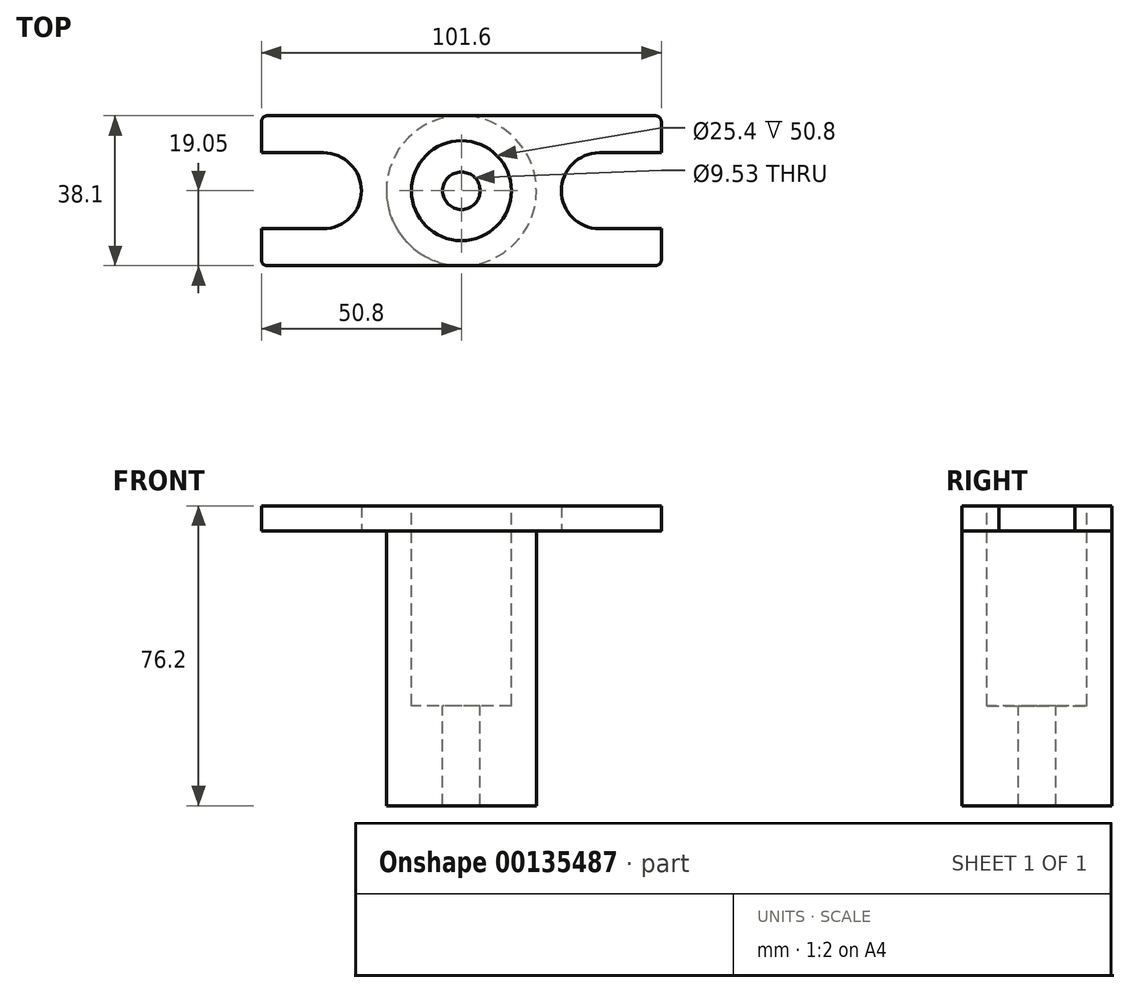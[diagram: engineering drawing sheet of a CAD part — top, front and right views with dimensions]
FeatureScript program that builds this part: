
annotation { "Feature Type Name" : "Feature", "Feature Type Description" : "" }
export const myFeature = defineFeature(function(context is Context, id is Id, definition is map)
    precondition{}
    {
        {
            var Q0;
            Q0=qCreatedBy(makeId("Top.planeOp"),FACE);
            var sketch = newSketch(context, id + "F0", { "sketchPlane" : qUnion([Q0])});
            skLineSegment(sketch, "E0.bottom", {"start": v(0, 0) * mm, "end": v(101.6, 0) * mm});
            skLineSegment(sketch, "E0.top", {"start": v(0, 38.1) * mm, "end": v(101.6, 38.1) * mm});
            skLineSegment(sketch, "E0.left", {"start": v(0, 0) * mm, "end": v(0, 9.4) * mm});
            skLineSegment(sketch, "E0.right", {"start": v(101.6, 0) * mm, "end": v(101.6, 9.4) * mm});
            skLineSegment(sketch, "E1.trimOffspring", {"start": v(0, 28.7) * mm, "end": v(0, 38.1) * mm});
            skLineSegment(sketch, "E2.trimOffspring", {"start": v(101.6, 28.7) * mm, "end": v(101.6, 38.1) * mm});
            skLineSegment(sketch, "E3.bottom", {"start": v(0, 28.7) * mm, "end": v(15.75, 28.7) * mm});
            skLineSegment(sketch, "E3.top", {"start": v(0, 9.4) * mm, "end": v(15.75, 9.4) * mm});
            skLineSegment(sketch, "E3.left", {"start": v(0, 28.7) * mm, "end": v(0, 9.4) * mm});
            skLineSegment(sketch, "E3.right", {"start": v(15.75, 28.7) * mm, "end": v(15.75, 9.4) * mm});
            skLineSegment(sketch, "E4.bottom", {"start": v(101.6, 28.7) * mm, "end": v(85.85, 28.7) * mm});
            skLineSegment(sketch, "E4.top", {"start": v(101.6, 9.4) * mm, "end": v(85.85, 9.4) * mm});
            skLineSegment(sketch, "E4.left", {"start": v(101.6, 28.7) * mm, "end": v(101.6, 9.4) * mm});
            skLineSegment(sketch, "E4.right", {"start": v(85.85, 28.7) * mm, "end": v(85.85, 9.4) * mm});
            skArc(sketch, "E5", {"start": v(15.75, 9.4) * mm, "mid": v(25.4, 19.05) * mm, "end": v(15.75, 28.7) * mm});
            skArc(sketch, "E6", {"start": v(85.85, 28.7) * mm, "mid": v(76.2, 19.05) * mm, "end": v(85.85, 9.4) * mm});
            skCircle(sketch, "E7", {"center": v(50.8, 19.93) * mm, "radius": 8.78 * mm, "construction": true});
            skSolve(sketch);
        }
        {
            var Q0;
            Q0=makeQuery(id+"F0.imprint","IMPRINT",FACE,{"disambiguationData":[TD([[makeQuery(id+"F0.imprint","IMPRINT",EDGE,{"derivedFrom":sQuery(id+"F0.wireOp",EDGE,"E0.bottom")}),1.0]])]});
            extrude(context, id + "F1", {"entities" : qUnion([Q0]), "depth" : 6.35 * mm});
        }
        {
            var Q0;
            Q0=makeQuery(id+"F1.opExtrude","CAP_FACE",FACE,{"disambiguationData":[OSD([sQuery(id+"F0.wireOp",EDGE,"E0.bottom"),sQuery(id+"F0.wireOp",EDGE,"E0.top"),sQuery(id+"F0.wireOp",EDGE,"E0.left"),sQuery(id+"F0.wireOp",EDGE,"E0.right"),sQuery(id+"F0.wireOp",EDGE,"So8w0W6L-Nd8J-bDPT-vjVD-5eYZ7nEJATCC"),sQuery(id+"F0.wireOp",EDGE,"ML5IMY0P-KDOL-A0Oi-dJc1-0zr9aFNHKgkh"),sQuery(id+"F0.wireOp",EDGE,"E1.trimOffspring"),sQuery(id+"F0.wireOp",EDGE,"E2.trimOffspring")])],"isStart":true});
            var sketch = newSketch(context, id + "F2", { "sketchPlane" : qUnion([Q0])});
            skCircle(sketch, "E8", {"center": v(50.8, -19.05) * mm, "radius": 19.05 * mm});
            skSolve(sketch);
        }
        {
            var Q0;
            Q0=makeQuery(id+"F2.imprint","IMPRINT",FACE,{"disambiguationData":[TD([[makeQuery(id+"F2.imprint","IMPRINT",EDGE,{"derivedFrom":sQuery(id+"F2.wireOp",EDGE,"E8")}),1.0]])]});
            extrude(context, id + "F3", {"entities" : qUnion([Q0]), "operationType" : NewBodyOperationType.ADD, "depth" : 69.85 * mm});
        }
        {
            var Q0;
            Q0=makeQuery(id+"F1.opExtrude","CAP_FACE",FACE,{"disambiguationData":[OSD([sQuery(id+"F0.wireOp",EDGE,"E0.bottom"),sQuery(id+"F0.wireOp",EDGE,"E0.top"),sQuery(id+"F0.wireOp",EDGE,"E0.left"),sQuery(id+"F0.wireOp",EDGE,"E0.right"),sQuery(id+"F0.wireOp",EDGE,"So8w0W6L-Nd8J-bDPT-vjVD-5eYZ7nEJATCC"),sQuery(id+"F0.wireOp",EDGE,"ML5IMY0P-KDOL-A0Oi-dJc1-0zr9aFNHKgkh"),sQuery(id+"F0.wireOp",EDGE,"E1.trimOffspring"),sQuery(id+"F0.wireOp",EDGE,"E2.trimOffspring")])],"isStart":false});
            var sketch = newSketch(context, id + "F4", { "sketchPlane" : qUnion([Q0])});
            skCircle(sketch, "E9", {"center": v(50.8, 19.05) * mm, "radius": 12.7 * mm});
            skCircle(sketch, "E10", {"center": v(50.8, 19.05) * mm, "radius": 4.76 * mm});
            skSolve(sketch);
        }
        {
            var Q0;
            Q0=makeQuery(id+"F4.imprint","IMPRINT",FACE,{"disambiguationData":[TD([[makeQuery(id+"F4.imprint","IMPRINT",EDGE,{"derivedFrom":sQuery(id+"F4.wireOp",EDGE,"E9")}),1.0]])]});
            extrude(context, id + "F5", {"entities" : qUnion([Q0]), "operationType" : NewBodyOperationType.REMOVE, "oppositeDirection" : true, "depth" : 50.8 * mm});
        }
        {
            var Q0;
            Q0=makeQuery(id+"F4.imprint","IMPRINT",FACE,{"disambiguationData":[TD([[makeQuery(id+"F4.imprint","IMPRINT",EDGE,{"derivedFrom":sQuery(id+"F4.wireOp",EDGE,"E10")}),1.0]])]});
            extrude(context, id + "F6", {"entities" : qUnion([Q0]), "operationType" : NewBodyOperationType.REMOVE, "endBound" : BoundingType.THROUGH_ALL, "oppositeDirection" : true, "depth" : 25.4 * mm});
        }
        {
            var Q0;
            Q0=makeQuery(id+"F1.opExtrude","SWEPT_EDGE",EDGE,{"disambiguationData":[OSD([sQuery(id+"F0.wireOp",EDGE,"E0.top"),sQuery(id+"F0.wireOp",EDGE,"E1.trimOffspring")])]});
            var Q1;
            Q1=makeQuery(id+"F1.opExtrude","SWEPT_EDGE",EDGE,{"disambiguationData":[OSD([sQuery(id+"F0.wireOp",EDGE,"E0.bottom"),sQuery(id+"F0.wireOp",EDGE,"E0.left")])]});
            var Q2;
            Q2=makeQuery(id+"F1.opExtrude","SWEPT_EDGE",EDGE,{"disambiguationData":[OSD([sQuery(id+"F0.wireOp",EDGE,"E0.bottom"),sQuery(id+"F0.wireOp",EDGE,"E0.right")])]});
            var Q3;
            Q3=makeQuery(id+"F1.opExtrude","SWEPT_EDGE",EDGE,{"disambiguationData":[OSD([sQuery(id+"F0.wireOp",EDGE,"E0.top"),sQuery(id+"F0.wireOp",EDGE,"E2.trimOffspring")])]});
            fillet(context, id + "F7", {"entities" : qUnion([Q0, Q1, Q2, Q3]), "radius" : 1.52 * mm, "tangentPropagation" : true, "allowEdgeOverflow" : false});
        }
    });
